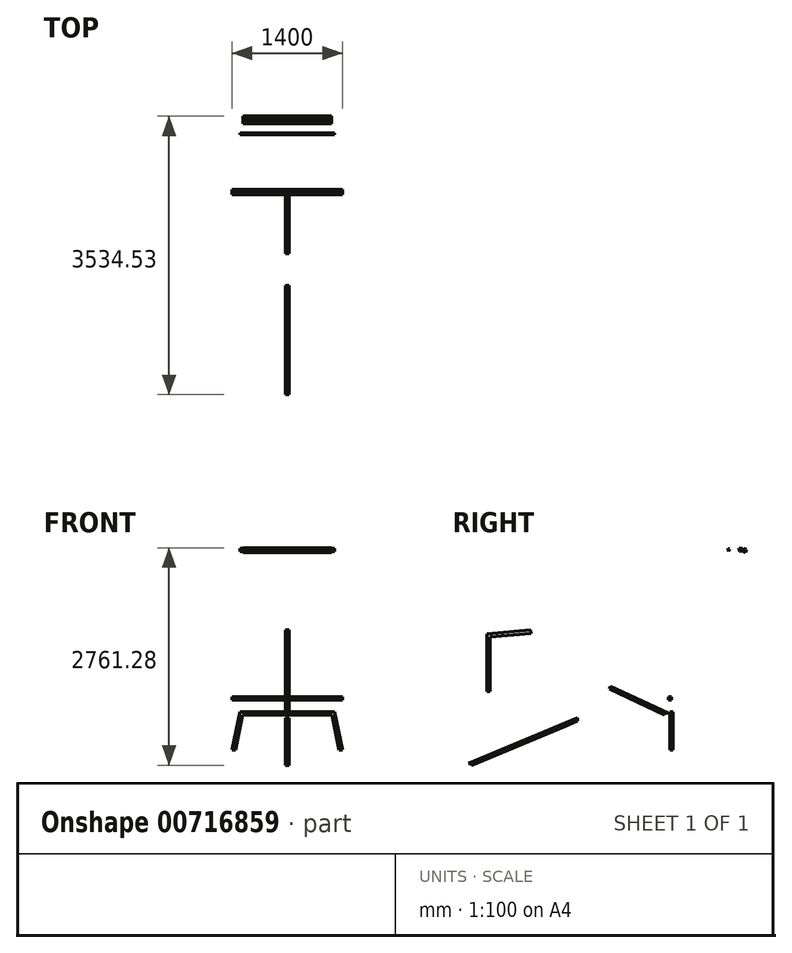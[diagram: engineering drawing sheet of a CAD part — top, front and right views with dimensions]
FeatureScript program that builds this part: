
annotation { "Feature Type Name" : "Feature", "Feature Type Description" : "" }
export const myFeature = defineFeature(function(context is Context, id is Id, definition is map)
    precondition{}
    {
        {
            var Q0;
            Q0=qCreatedBy(makeId("Right.planeOp"),FACE);
            var sketch = newSketch(context, id + "F0", { "sketchPlane" : qUnion([Q0])});
            skLineSegment(sketch, "E0.bottom", {"start": v(398.6, 562.32) * mm, "end": v(438.6, 562.32) * mm});
            skLineSegment(sketch, "E0.top", {"start": v(398.6, 1042.32) * mm, "end": v(438.6, 1042.32) * mm});
            skLineSegment(sketch, "E0.left", {"start": v(398.6, 562.32) * mm, "end": v(398.6, 1042.32) * mm});
            skLineSegment(sketch, "E0.right", {"start": v(438.6, 562.32) * mm, "end": v(438.6, 1042.32) * mm});
            skLineSegment(sketch, "E1", {"start": v(438.6, 1042.32) * mm, "end": v(-286.44, 1380.42) * mm});
            skLineSegment(sketch, "E2.0", {"start": v(398.6, 1016.84) * mm, "end": v(-303.68, 1344.32) * mm});
            skLineSegment(sketch, "E3", {"start": v(-303.68, 1344.32) * mm, "end": v(-286.44, 1380.42) * mm});
            skLineSegment(sketch, "E4.bottom", {"start": v(398.6, 562.32) * mm, "end": v(-861.4, 562.32) * mm});
            skLineSegment(sketch, "E4.top", {"start": v(398.6, 602.32) * mm, "end": v(-861.4, 602.32) * mm});
            skLineSegment(sketch, "E4.left", {"start": v(398.6, 562.32) * mm, "end": v(398.6, 602.32) * mm});
            skLineSegment(sketch, "E4.right", {"start": v(-861.4, 562.32) * mm, "end": v(-861.4, 602.32) * mm});
            skLineSegment(sketch, "E5", {"start": v(-861.4, 602.32) * mm, "end": v(-861.4, 1335.68) * mm});
            skLineSegment(sketch, "E6", {"start": v(-303.68, 1344.32) * mm, "end": v(-861.4, 1295.52) * mm});
            skLineSegment(sketch, "E7.0", {"start": v(-307.16, 1384.17) * mm, "end": v(-861.4, 1335.68) * mm});
            skLineSegment(sketch, "E8", {"start": v(-307.16, 1384.17) * mm, "end": v(-303.68, 1344.32) * mm});
            skLineSegment(sketch, "E9", {"start": v(-307.16, 1384.17) * mm, "end": v(-286.44, 1380.42) * mm});
            skLineSegment(sketch, "E10.0", {"start": v(-821.4, 602.32) * mm, "end": v(-821.4, 1339.18) * mm});
            skSolve(sketch);
        }
        {
            var Q0;
            Q0=qCreatedBy(makeId("Front.planeOp"),FACE);
            var sketch = newSketch(context, id + "F1", { "sketchPlane" : qUnion([Q0])});
            skLineSegment(sketch, "E11.top", {"start": v(600, -20) * mm, "end": v(567.47, -20) * mm});
            skLineSegment(sketch, "E11.right", {"start": v(-600, 20) * mm, "end": v(-600, -20) * mm});
            skPoint(sketch, "E11.middle", {"position": v(0, 0) * mm});
            skLineSegment(sketch, "E12.bottom", {"start": v(-600, -20) * mm, "end": v(-567.47, -20) * mm});
            skLineSegment(sketch, "E13.bottom", {"start": v(-659.14, -460) * mm, "end": v(-700, -460) * mm});
            skLineSegment(sketch, "E14.bottom", {"start": v(659.14, -460) * mm, "end": v(700, -460) * mm});
            skLineSegment(sketch, "E15", {"start": v(600, 20) * mm, "end": v(700, -460) * mm});
            skLineSegment(sketch, "E16", {"start": v(-600, 20) * mm, "end": v(-700, -460) * mm});
            skLineSegment(sketch, "E17.0", {"start": v(-567.47, -20) * mm, "end": v(-659.14, -460) * mm});
            skLineSegment(sketch, "E18.0", {"start": v(567.47, -20) * mm, "end": v(659.14, -460) * mm});
            skLineSegment(sketch, "E19.trimOffspring", {"start": v(-567.47, -20) * mm, "end": v(-600, -20) * mm});
            skLineSegment(sketch, "E20", {"start": v(600, 20) * mm, "end": v(600, -20) * mm});
            skLineSegment(sketch, "E21", {"start": v(-600, 20) * mm, "end": v(600, 20) * mm});
            skLineSegment(sketch, "E22", {"start": v(567.47, -20) * mm, "end": v(-567.47, -20) * mm});
            skSolve(sketch);
        }
        {
            var Q0;
            Q0 = qSketchRegion(id + "F1", true);
            extrude(context, id + "F2", {"entities" : qUnion([Q0]), "endBound" : BoundingType.SYMMETRIC, "depth" : 40 * mm, "offsetDistance" : 25 * mm});
        }
        {
            var Q0;
            Q0=qCreatedBy(makeId("Right.planeOp"),FACE);
            var sketch = newSketch(context, id + "F3", { "sketchPlane" : qUnion([Q0])});
            skLineSegment(sketch, "E23.bottom", {"start": v(-47.5, 8.91) * mm, "end": v(-87.5, 8.91) * mm});
            skLineSegment(sketch, "E23.right", {"start": v(-87.5, 8.91) * mm, "end": v(-87.5, -16.57) * mm});
            skLineSegment(sketch, "E24", {"start": v(-47.5, 8.91) * mm, "end": v(-772.54, 347) * mm});
            skLineSegment(sketch, "E25.0", {"start": v(-87.5, -16.57) * mm, "end": v(-789.44, 310.76) * mm});
            skLineSegment(sketch, "E26", {"start": v(-789.44, 310.76) * mm, "end": v(-772.54, 347) * mm});
            skSolve(sketch);
        }
        {
            var Q0;
            Q0 = qSketchRegion(id + "F3", true);
            extrude(context, id + "F4", {"entities" : qUnion([Q0]), "endBound" : BoundingType.SYMMETRIC, "depth" : 40 * mm, "offsetDistance" : 25 * mm});
        }
        {
            var Q0;
            Q0=qCreatedBy(makeId("Right.planeOp"),FACE);
            var sketch = newSketch(context, id + "F5", { "sketchPlane" : qUnion([Q0])});
            skLineSegment(sketch, "E27", {"start": v(721.74, 2057.2) * mm, "end": v(738.98, 2093.3) * mm});
            skLineSegment(sketch, "E28", {"start": v(718.25, 2097.05) * mm, "end": v(721.74, 2057.2) * mm});
            skLineSegment(sketch, "E29", {"start": v(718.25, 2097.05) * mm, "end": v(738.98, 2093.3) * mm});
            skSolve(sketch);
        }
        {
            var Q0;
            Q0 = qSketchRegion(id + "F5", true);
            extrude(context, id + "F6", {"entities" : qUnion([Q0]), "endBound" : BoundingType.SYMMETRIC, "depth" : 1200 * mm, "offsetDistance" : 25 * mm});
        }
        {
            var Q0;
            Q0=makeQuery(id+"F0.imprint","IMPRINT",FACE,{"disambiguationData":[TD([[makeQuery(id+"F0.imprint","IMPRINT",EDGE,{"derivedFrom":sQuery(id+"F0.wireOp",EDGE,"E3")}),1.0]])]});
            var sketch = newSketch(context, id + "F7", { "sketchPlane" : qUnion([Q0])});
            skLineSegment(sketch, "E30", {"start": v(899.79, 2063.66) * mm, "end": v(917.02, 2099.76) * mm});
            skLineSegment(sketch, "E31", {"start": v(896.3, 2103.51) * mm, "end": v(899.79, 2063.66) * mm});
            skLineSegment(sketch, "E32.0", {"start": v(935.88, 2046.43) * mm, "end": v(953.12, 2082.53) * mm});
            skLineSegment(sketch, "E33", {"start": v(917.02, 2099.76) * mm, "end": v(953.12, 2082.53) * mm});
            skLineSegment(sketch, "E34", {"start": v(899.79, 2063.66) * mm, "end": v(935.88, 2046.43) * mm});
            skLineSegment(sketch, "E35.0", {"start": v(856.45, 2100.03) * mm, "end": v(859.94, 2060.18) * mm});
            skLineSegment(sketch, "E36", {"start": v(856.45, 2100.03) * mm, "end": v(896.3, 2103.51) * mm});
            skLineSegment(sketch, "E37", {"start": v(899.79, 2063.66) * mm, "end": v(859.94, 2060.18) * mm});
            skSolve(sketch);
        }
        {
            var Q0;
            Q0 = qSketchRegion(id + "F7", true);
            extrude(context, id + "F8", {"entities" : qUnion([Q0]), "endBound" : BoundingType.SYMMETRIC, "depth" : 1120 * mm, "offsetDistance" : 25 * mm});
        }
        {
            var Q0;
            Q0=qCreatedBy(makeId("Right.planeOp"),FACE);
            var sketch = newSketch(context, id + "F9", { "sketchPlane" : qUnion([Q0])});
            skLineSegment(sketch, "E38", {"start": v(-2345.38, 277.9) * mm, "end": v(-2345.38, 1011.26) * mm});
            skLineSegment(sketch, "E39", {"start": v(-1787.66, 1019.9) * mm, "end": v(-2345.38, 971.1) * mm});
            skLineSegment(sketch, "E40.0", {"start": v(-1791.15, 1059.75) * mm, "end": v(-2345.38, 1011.26) * mm});
            skLineSegment(sketch, "E41", {"start": v(-1791.15, 1059.75) * mm, "end": v(-1787.66, 1019.9) * mm});
            skLineSegment(sketch, "E42.0", {"start": v(-2305.38, 277.9) * mm, "end": v(-2305.38, 1014.76) * mm});
            skLineSegment(sketch, "E43", {"start": v(-2345.38, 277.9) * mm, "end": v(-2305.38, 277.9) * mm});
            skSolve(sketch);
        }
        {
            var Q0;
            Q0 = qSketchRegion(id + "F9", true);
            extrude(context, id + "F10", {"entities" : qUnion([Q0]), "endBound" : BoundingType.SYMMETRIC, "depth" : 40 * mm, "offsetDistance" : 25 * mm});
        }
        {
            var Q0;
            Q0=qCreatedBy(makeId("Right.planeOp"),FACE);
            var sketch = newSketch(context, id + "F11", { "sketchPlane" : qUnion([Q0])});
            skLineSegment(sketch, "E44.bottom", {"start": v(-40, 209.84) * mm, "end": v(0, 209.84) * mm});
            skLineSegment(sketch, "E44.top", {"start": v(-40, 169.84) * mm, "end": v(0, 169.84) * mm});
            skLineSegment(sketch, "E44.left", {"start": v(-40, 209.84) * mm, "end": v(-40, 169.84) * mm});
            skLineSegment(sketch, "E44.right", {"start": v(0, 209.84) * mm, "end": v(0, 169.84) * mm});
            skSolve(sketch);
        }
        {
            var Q0;
            Q0 = qSketchRegion(id + "F11", true);
            extrude(context, id + "F12", {"entities" : qUnion([Q0]), "endBound" : BoundingType.SYMMETRIC, "depth" : 1400 * mm, "offsetDistance" : 25 * mm});
        }
        {
            var Q0;
            Q0=qCreatedBy(makeId("Right.planeOp"),FACE);
            var sketch = newSketch(context, id + "F13", { "sketchPlane" : qUnion([Q0])});
            skLineSegment(sketch, "E45.top", {"start": v(-2581.41, -631.12) * mm, "end": v(-2541.41, -631.12) * mm});
            skLineSegment(sketch, "E46.left", {"start": v(-1351.41, -161.1) * mm, "end": v(-1197.14, -93.37) * mm});
            skLineSegment(sketch, "E47.left", {"start": v(-1197.14, -93.37) * mm, "end": v(-1197.14, -53.37) * mm});
            skLineSegment(sketch, "E48", {"start": v(-2581.41, -631.12) * mm, "end": v(-1197.14, -53.37) * mm});
            skLineSegment(sketch, "E49.0", {"start": v(-2541.41, -657.77) * mm, "end": v(-1351.41, -161.1) * mm});
            skLineSegment(sketch, "E50.trimOffspring", {"start": v(-2541.41, -657.77) * mm, "end": v(-2541.41, -631.12) * mm});
            skSolve(sketch);
        }
        {
            var Q0;
            Q0=makeQuery(id+"F13.imprint","IMPRINT",FACE,{"disambiguationData":[TD([[makeQuery(id+"F13.imprint","IMPRINT",EDGE,{"derivedFrom":sQuery(id+"F13.wireOp",EDGE,"E45.top")}),1.0]])]});
            extrude(context, id + "F14", {"entities" : qUnion([Q0]), "endBound" : BoundingType.SYMMETRIC, "depth" : 40 * mm, "offsetDistance" : 25 * mm});
        }
    });
